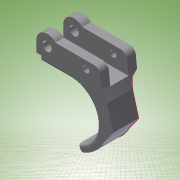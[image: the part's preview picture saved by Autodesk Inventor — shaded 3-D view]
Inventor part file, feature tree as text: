
AUTODESK INVENTOR PART (.ipt)
format: ipt  version: 2011 (Build 150239000, 239)  size: 282,624 bytes
history: native  units: in
note: dims shown in document units (in); Inventor stores cm internally (conversion verified against a paired STEP export)
features: sketch x12, extrude x10, fillet x5, hole x2, chamfer x2
ambient origin geometry x8: Origin, YZ Plane, XZ Plane, XY Plane, X Axis, Y Axis, Z Axis, Center Point
bodies: Solid1 (feature_tree)
feature tree (31):
  extrude  "Extrusion1"  Depth=1.0in
  extrude  "Extrusion2"  Depth=0.875in
  extrude  "Extrusion3"  Depth=0.308in
  extrude  "Extrusion4"  Depth=0.0725in TaperAngle=0.0deg
  hole  "Hole1"  [1 undecoded]
  hole  "Hole2"  [1 undecoded]
  extrude  "Extrusion5"  Depth=0.108in
  extrude  "Extrusion6"  Depth=0.0725in TaperAngle=0.0deg
  extrude  "Extrusion7"  Depth=0.438in
  extrude  "Extrusion8"  Depth=0.0725in TaperAngle=0.0deg
  extrude  "Extrusion9"  Depth=0.0725in TaperAngle=0.0deg
  fillet  "Fillet1"  Radius=0.125in
  fillet  "Fillet2"  Radius=0.1265in
  chamfer  "Chamfer1"  Distance=0.1265in
  chamfer  "Chamfer2"  Distance=0.0725in
  fillet  "Fillet3"  Radius=0.085in
  fillet  "Fillet4"  Radius=0.0312in
  fillet  "Fillet5"  Radius=0.0625in
  extrude  "Extrusion10"  Depth=0.0625in TaperAngle=45.0deg
  sketch  "Sketch1"  dims[d0=1.355in d1=1.0in]
  sketch  "Sketch2"  dims[d2=0.493in d3=0.0in d4=0.875in]
  sketch  "Sketch3"  dims[d5=0.357in d7=0.308in]
  sketch  "Sketch4"  dims[d8=0.302in d9=0.0725in d10=0.0in]
  sketch  "Sketch5"  dims[d12=0.75in d13=0.0725in d14=0.0in]
  sketch  "Sketch6"  dims[d15=0.0725in d16=0.0in]
  sketch  "Sketch7"  dims[d17=0.125in d18=0.5in d19=0.375in d20=0.25in d21=0.5635in d22=0.75in d23=0.8108in d24=0.54in]
  sketch  "Sketch8"  dims[d25=0.085in d26=0.5in d27=0.375in d28=0.25in d29=0.5635in d30=0.75in d31=0.8108in d32=0.108in]
  sketch  "Sketch9"  dims[d33=0.25in d34=0.0725in d35=0.0in]
  sketch  "Sketch10"  dims[d36=0.0725in d37=0.0in d39=0.438in]
  sketch  "Sketch11"  dims[d41=0.375in d42=0.0725in d43=0.0in]
  sketch  "Sketch13"  dims[d44=0.0725in d45=0.0725in d46=0.0in d47=0.125in d48=0.1265in d50=0.1265in d51=0.0725in d52=0.0in d53=0.085in d54=0.0312in d55=0.0625in d56=0.125in d57=45.0deg d58=0.0625in d59=0.125in d60=45.0deg d61=0.0312in d62=0.0312in d63=0.0312in d64=1.0in d65=0.0in]
note: 2 required parameter values undecoded (feature->parameter linkage not recoverable at this tier; creation-order binding heuristic only, values carry confidence <= 0.55)
